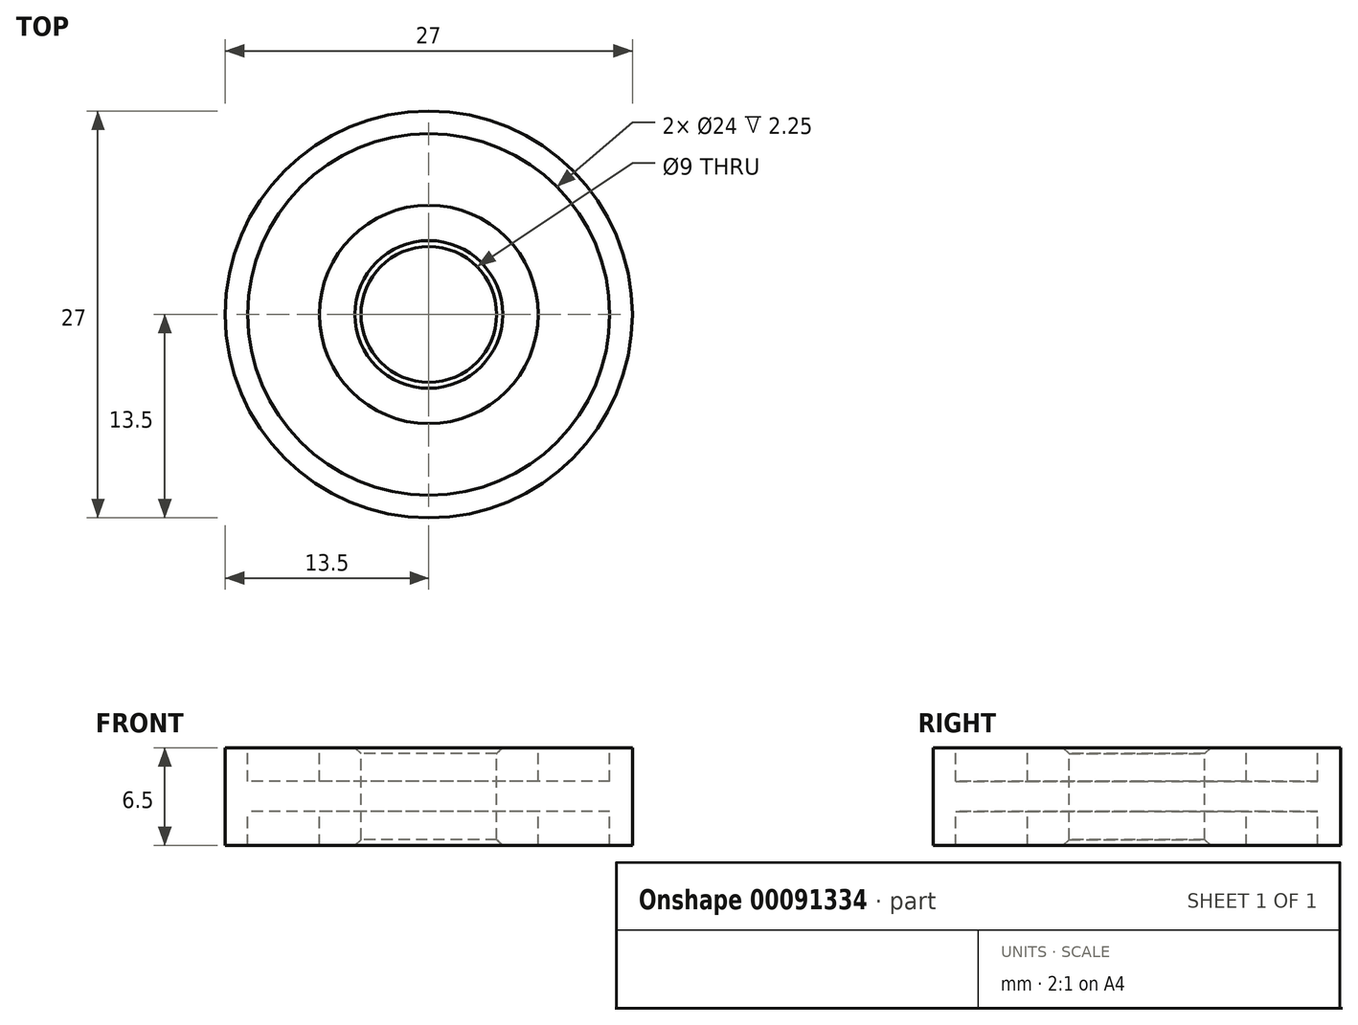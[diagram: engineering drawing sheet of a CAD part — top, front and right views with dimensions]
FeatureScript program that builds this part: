
annotation { "Feature Type Name" : "Feature", "Feature Type Description" : "" }
export const myFeature = defineFeature(function(context is Context, id is Id, definition is map)
    precondition{}
    {
        {
            var Q0;
            Q0=qCreatedBy(makeId("Front.planeOp"),FACE);
            var sketch = newSketch(context, id + "F0", { "sketchPlane" : qUnion([Q0])});
            skLineSegment(sketch, "E0.bottom", {"start": v(13.5, 3.25) * mm, "end": v(-13.5, 3.25) * mm});
            skLineSegment(sketch, "E0.top", {"start": v(13.5, -3.25) * mm, "end": v(-13.5, -3.25) * mm});
            skLineSegment(sketch, "E0.left", {"start": v(13.5, 3.25) * mm, "end": v(13.5, -3.25) * mm});
            skLineSegment(sketch, "E0.right", {"start": v(-13.5, 3.25) * mm, "end": v(-13.5, -3.25) * mm});
            skPoint(sketch, "E0.middle", {"position": v(0, 0) * mm});
            skLineSegment(sketch, "E1.bottom", {"start": v(4.5, 3.25) * mm, "end": v(-4.5, 3.25) * mm});
            skLineSegment(sketch, "E1.top", {"start": v(4.5, -3.25) * mm, "end": v(-4.5, -3.25) * mm});
            skLineSegment(sketch, "E1.left", {"start": v(4.5, 3.25) * mm, "end": v(4.5, -3.25) * mm});
            skLineSegment(sketch, "E1.right", {"start": v(-4.5, 3.25) * mm, "end": v(-4.5, -3.25) * mm});
            skLineSegment(sketch, "E2.bottom", {"start": v(12, 3.25) * mm, "end": v(-12, 3.25) * mm});
            skLineSegment(sketch, "E2.top", {"start": v(12, -3.25) * mm, "end": v(-12, -3.25) * mm});
            skLineSegment(sketch, "E2.left", {"start": v(12, 3.25) * mm, "end": v(12, -3.25) * mm});
            skLineSegment(sketch, "E2.right", {"start": v(-12, 3.25) * mm, "end": v(-12, -3.25) * mm});
            skLineSegment(sketch, "E3.bottom", {"start": v(7.25, 3.25) * mm, "end": v(-7.25, 3.25) * mm});
            skLineSegment(sketch, "E3.top", {"start": v(7.25, -3.25) * mm, "end": v(-7.25, -3.25) * mm});
            skLineSegment(sketch, "E3.left", {"start": v(7.25, 3.25) * mm, "end": v(7.25, -3.25) * mm});
            skLineSegment(sketch, "E3.right", {"start": v(-7.25, 3.25) * mm, "end": v(-7.25, -3.25) * mm});
            skLineSegment(sketch, "E4", {"start": v(-13.5, 1) * mm, "end": v(13.5, 1) * mm});
            skLineSegment(sketch, "E5", {"start": v(-13.5, -1) * mm, "end": v(13.5, -1) * mm});
            skLineSegment(sketch, "E6", {"start": v(0, 13.08) * mm, "end": v(0, -14.95) * mm});
            skSolve(sketch);
        }
        {
            var Q0;
            {var subQ0=sQuery(id+"F0.wireOp",EDGE,"E0.right");var subQ1=sQuery(id+"F0.wireOp",EDGE,"E0.bottom");var subQ2=makeQuery(id+"F0.imprint","INTERSECT",VERTEX,{"derivedFrom":[subQ1,subQ0]});Q0=makeQuery(id+"F0.imprint","IMPRINT",FACE,{"disambiguationData":[TD([[makeQuery(id+"F0.imprint","IMPRINT",EDGE,{"disambiguationData":[TD([[subQ2,-1.0]])],"derivedFrom":subQ0}),1.0]])]});}
            var Q1;
            {var subQ0=sQuery(id+"F0.wireOp",EDGE,"E4");var subQ1=sQuery(id+"F0.wireOp",EDGE,"E0.right");var subQ2=makeQuery(id+"F0.imprint","INTERSECT",VERTEX,{"derivedFrom":[subQ1,subQ0]});Q1=makeQuery(id+"F0.imprint","IMPRINT",FACE,{"disambiguationData":[TD([[makeQuery(id+"F0.imprint","IMPRINT",EDGE,{"disambiguationData":[TD([[subQ2,-1.0]])],"derivedFrom":subQ1}),1.0]])]});}
            var Q2;
            {var subQ0=sQuery(id+"F0.wireOp",EDGE,"E0.right");var subQ1=sQuery(id+"F0.wireOp",EDGE,"E0.top");var subQ2=makeQuery(id+"F0.imprint","INTERSECT",VERTEX,{"derivedFrom":[subQ1,subQ0]});Q2=makeQuery(id+"F0.imprint","IMPRINT",FACE,{"disambiguationData":[TD([[makeQuery(id+"F0.imprint","IMPRINT",EDGE,{"disambiguationData":[TD([[subQ2,1.0]])],"derivedFrom":subQ0}),1.0]])]});}
            var Q3;
            {var subQ0=sQuery(id+"F0.wireOp",EDGE,"E4");var subQ1=sQuery(id+"F0.wireOp",EDGE,"E2.right");var subQ2=makeQuery(id+"F0.imprint","INTERSECT",VERTEX,{"derivedFrom":[subQ1,subQ0]});Q3=makeQuery(id+"F0.imprint","IMPRINT",FACE,{"disambiguationData":[TD([[makeQuery(id+"F0.imprint","IMPRINT",EDGE,{"disambiguationData":[TD([[subQ2,-1.0]])],"derivedFrom":subQ1}),1.0]])]});}
            var Q4;
            {var subQ0=sQuery(id+"F0.wireOp",EDGE,"E3.bottom");var subQ1=sQuery(id+"F0.wireOp",EDGE,"E1.right");var subQ2=makeQuery(id+"F0.imprint","INTERSECT",VERTEX,{"derivedFrom":[subQ1,subQ0]});Q4=makeQuery(id+"F0.imprint","IMPRINT",FACE,{"disambiguationData":[TD([[makeQuery(id+"F0.imprint","IMPRINT",EDGE,{"disambiguationData":[TD([[subQ2,-1.0]])],"derivedFrom":subQ1}),-1.0]])]});}
            var Q5;
            {var subQ0=sQuery(id+"F0.wireOp",EDGE,"E4");var subQ1=sQuery(id+"F0.wireOp",EDGE,"E1.right");var subQ2=makeQuery(id+"F0.imprint","INTERSECT",VERTEX,{"derivedFrom":[subQ1,subQ0]});Q5=makeQuery(id+"F0.imprint","IMPRINT",FACE,{"disambiguationData":[TD([[makeQuery(id+"F0.imprint","IMPRINT",EDGE,{"disambiguationData":[TD([[subQ2,-1.0]])],"derivedFrom":subQ1}),-1.0]])]});}
            var Q6;
            {var subQ0=sQuery(id+"F0.wireOp",EDGE,"E3.top");var subQ1=sQuery(id+"F0.wireOp",EDGE,"E1.right");var subQ2=makeQuery(id+"F0.imprint","INTERSECT",VERTEX,{"derivedFrom":[subQ1,subQ0]});Q6=makeQuery(id+"F0.imprint","IMPRINT",FACE,{"disambiguationData":[TD([[makeQuery(id+"F0.imprint","IMPRINT",EDGE,{"disambiguationData":[TD([[subQ2,1.0]])],"derivedFrom":subQ1}),-1.0]])]});}
            var Q7;
            Q7=sQuery(id+"F0.wireOp",EDGE,"E6");
            revolve(context, id + "F1", {"entities" : qUnion([Q0, Q1, Q2, Q3, Q4, Q5, Q6]), "axis" : qUnion([Q7]), "revolveType" : RevolveType.FULL});
        }
        {
            var Q0;
            Q0=makeQuery(id+"F1.opRevolve","SWEPT_EDGE",EDGE,{"disambiguationData":[OSD([sQuery(id+"F0.wireOp",EDGE,"E1.right"),sQuery(id+"F0.wireOp",EDGE,"E3.bottom")])]});
            var Q1;
            Q1=makeQuery(id+"F1.opRevolve","SWEPT_EDGE",EDGE,{"disambiguationData":[OSD([sQuery(id+"F0.wireOp",EDGE,"E1.right"),sQuery(id+"F0.wireOp",EDGE,"E3.top")])]});
            chamfer(context, id + "F2", {"entities" : qUnion([Q0, Q1]), "width" : .4 * mm, "tangentPropagation" : true});
        }
    });
